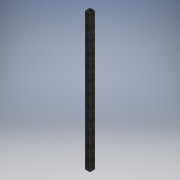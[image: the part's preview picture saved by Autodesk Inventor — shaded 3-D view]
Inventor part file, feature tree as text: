
AUTODESK INVENTOR PART (.ipt)
format: ipt  version: 2017 (Build 210142000, 142)  size: 104,960 bytes
history: native  units: mm
features: other x1, extrude x1, sketch x1
ambient origin geometry x8: Origin, YZ Plane, XZ Plane, XY Plane, X Axis, Y Axis, Z Axis, Center Point
bodies: Body1 (feature_tree)
feature tree (3):
  other  "Sólido1"
  extrude  "Extrusión1"  Depth=75.0mm
  sketch  "Boceto1"  dims[d0=75.0mm d1=75.0mm d2=3.0mm d3=37.5mm d4=37.5mm d5=2100.0mm d6=0.0mm d7=1050.0mm d8=0.0mm]
